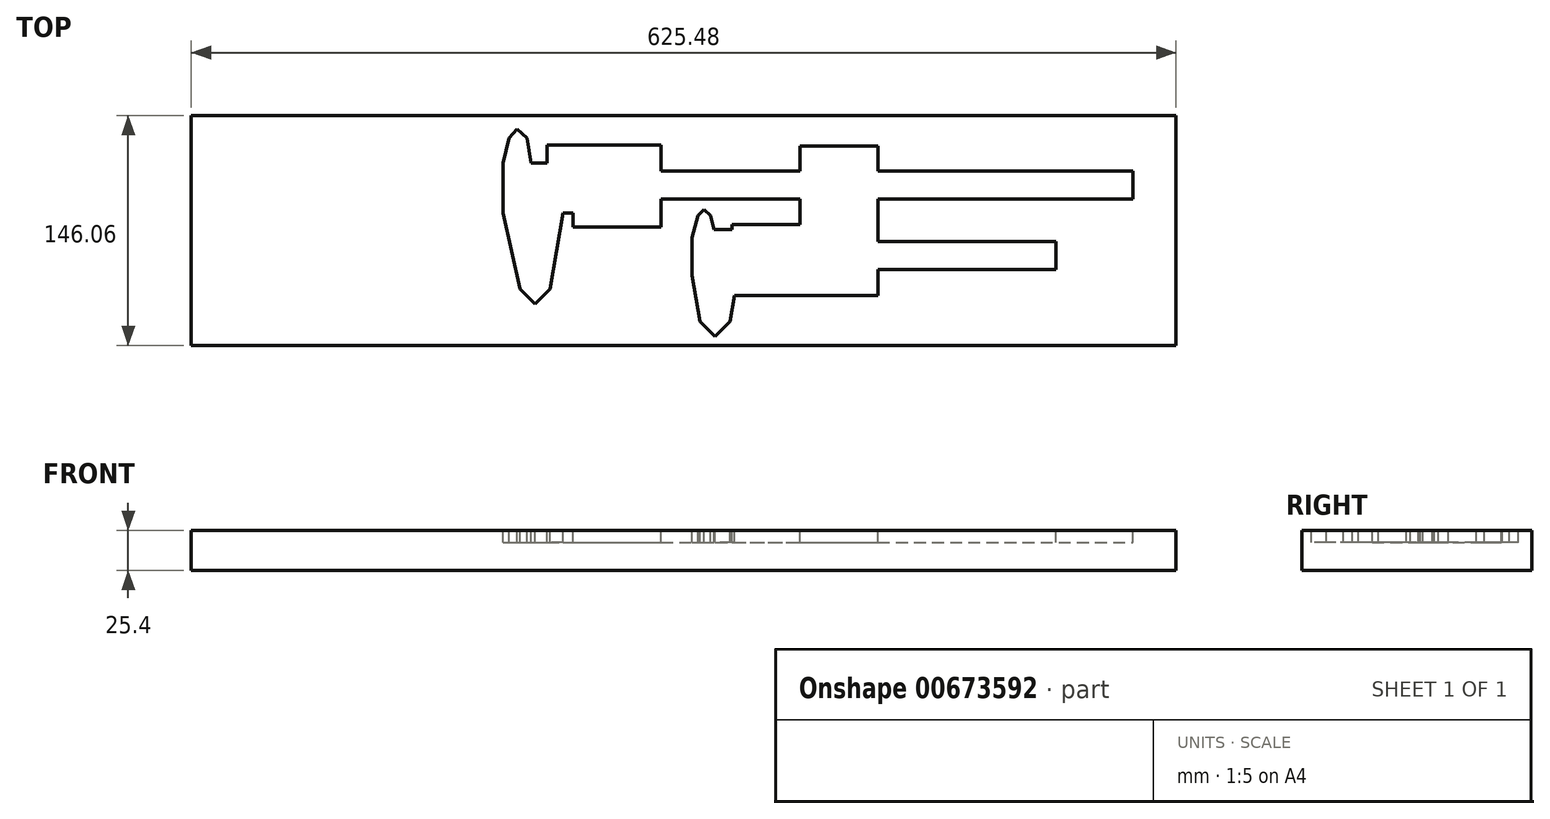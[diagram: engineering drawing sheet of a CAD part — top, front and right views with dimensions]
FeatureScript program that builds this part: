
annotation { "Feature Type Name" : "Feature", "Feature Type Description" : "" }
export const myFeature = defineFeature(function(context is Context, id is Id, definition is map)
    precondition{}
    {
        {
            var Q0;
            Q0=qCreatedBy(makeId("Top.planeOp"),FACE);
            var sketch = newSketch(context, id + "F0", { "sketchPlane" : qUnion([Q0])});
            skLineSegment(sketch, "E0.bottom", {"start": v(312.74, 73.03) * mm, "end": v(-312.74, 73.03) * mm});
            skLineSegment(sketch, "E0.top", {"start": v(312.74, -73.02) * mm, "end": v(-312.74, -73.02) * mm});
            skLineSegment(sketch, "E0.left", {"start": v(312.74, 73.03) * mm, "end": v(312.74, -73.02) * mm});
            skLineSegment(sketch, "E0.right", {"start": v(-312.74, 73.03) * mm, "end": v(-312.74, -73.02) * mm});
            skPoint(sketch, "E0.middle", {"position": v(0, 0) * mm});
            skSolve(sketch);
        }
        {
            var Q0;
            Q0=qCreatedBy(makeId("Top.planeOp"),FACE);
            var sketch = newSketch(context, id + "F1", { "sketchPlane" : qUnion([Q0])});
            skLineSegment(sketch, "E1", {"start": v(10.22, -57.71) * mm, "end": v(29.27, -57.71) * mm, "construction": true});
            skLineSegment(sketch, "E2", {"start": v(10.22, -57.71) * mm, "end": v(19.75, -67.24) * mm});
            skPoint(sketch, "E2.endSnap0", {"position": v(19.75, -57.71) * mm});
            skLineSegment(sketch, "E3", {"start": v(19.75, -67.24) * mm, "end": v(29.27, -57.71) * mm});
            skPoint(sketch, "E4", {"position": v(34.35, -28.5) * mm});
            skPoint(sketch, "E5", {"position": v(5.14, -28.5) * mm});
            skLineSegment(sketch, "E6", {"start": v(5.14, -28.5) * mm, "end": v(10.22, -57.71) * mm});
            skLineSegment(sketch, "E7", {"start": v(34.35, -28.5) * mm, "end": v(29.27, -57.71) * mm});
            skLineSegment(sketch, "E8", {"start": v(5.14, -28.5) * mm, "end": v(5.14, -4.37) * mm});
            skLineSegment(sketch, "E9", {"start": v(5.14, -4.37) * mm, "end": v(9.22, 9.6) * mm});
            skLineSegment(sketch, "E10", {"start": v(9.22, 9.6) * mm, "end": v(12.76, 13.4) * mm});
            skLineSegment(sketch, "E11", {"start": v(12.76, 13.4) * mm, "end": v(16.84, 9.6) * mm});
            skLineSegment(sketch, "E12", {"start": v(16.84, 9.6) * mm, "end": v(20.38, -4.37) * mm});
            skPoint(sketch, "E13", {"position": v(12.76, -4.37) * mm});
            skLineSegment(sketch, "E14", {"start": v(30.54, 3.75) * mm, "end": v(123.25, 3.75) * mm});
            skLineSegment(sketch, "E15", {"start": v(32.14, -41.2) * mm, "end": v(123.25, -41.2) * mm});
            skLineSegment(sketch, "E16.bottom", {"start": v(123.25, -6.91) * mm, "end": v(236.28, -6.91) * mm});
            skLineSegment(sketch, "E16.top", {"start": v(123.25, -24.7) * mm, "end": v(236.28, -24.7) * mm});
            skLineSegment(sketch, "E16.right", {"start": v(236.28, -6.91) * mm, "end": v(236.28, -24.7) * mm});
            skPoint(sketch, "E17", {"position": v(30.54, -4.37) * mm});
            skLineSegment(sketch, "E18", {"start": v(20.38, -4.37) * mm, "end": v(30.54, -4.37) * mm});
            skLineSegment(sketch, "E19", {"start": v(30.54, -4.37) * mm, "end": v(30.54, 3.75) * mm});
            skLineSegment(sketch, "E20", {"start": v(123.25, 3.75) * mm, "end": v(123.25, -6.91) * mm});
            skLineSegment(sketch, "E21", {"start": v(123.25, -24.7) * mm, "end": v(123.25, -41.2) * mm});
            skPoint(sketch, "E22", {"position": v(19.75, -28.5) * mm});
            skLineSegment(sketch, "E23", {"start": v(30.54, 0.7) * mm, "end": v(19.1, 0.7) * mm});
            skPoint(sketch, "E24", {"position": v(19.1, 0.7) * mm});
            skPoint(sketch, "E25", {"position": v(32.14, -41.2) * mm});
            skPoint(sketch, "E26", {"position": v(30.54, 0.7) * mm});
            skSolve(sketch);
        }
        {
            var Q0;
            Q0=qCreatedBy(makeId("Top.planeOp"),FACE);
            var sketch = newSketch(context, id + "F2", { "sketchPlane" : qUnion([Q0])});
            skLineSegment(sketch, "E27", {"start": v(-104.01, -37.14) * mm, "end": v(-84.96, -37.14) * mm, "construction": true});
            skLineSegment(sketch, "E28", {"start": v(-104.01, -37.14) * mm, "end": v(-94.49, -46.67) * mm});
            skPoint(sketch, "E28.endSnap0", {"position": v(-94.49, -37.14) * mm});
            skLineSegment(sketch, "E29", {"start": v(-94.49, -46.67) * mm, "end": v(-84.96, -37.14) * mm});
            skPoint(sketch, "E30", {"position": v(-76.54, 11.12) * mm});
            skPoint(sketch, "E31", {"position": v(-114.64, 11.12) * mm});
            skLineSegment(sketch, "E32", {"start": v(-114.64, 11.12) * mm, "end": v(-104.01, -37.14) * mm});
            skLineSegment(sketch, "E33", {"start": v(-76.54, 11.12) * mm, "end": v(-84.96, -37.14) * mm});
            skLineSegment(sketch, "E34", {"start": v(-114.64, 11.12) * mm, "end": v(-114.64, 42.87) * mm});
            skLineSegment(sketch, "E35", {"start": v(-114.64, 42.87) * mm, "end": v(-111.06, 58.76) * mm});
            skLineSegment(sketch, "E36", {"start": v(-111.06, 58.76) * mm, "end": v(-105.75, 64.46) * mm});
            skLineSegment(sketch, "E37", {"start": v(-105.75, 64.46) * mm, "end": v(-99.63, 58.76) * mm});
            skLineSegment(sketch, "E38", {"start": v(-99.63, 58.76) * mm, "end": v(-96.86, 42.87) * mm});
            skPoint(sketch, "E39", {"position": v(-105.75, 42.87) * mm});
            skLineSegment(sketch, "E40", {"start": v(-86.7, 54.3) * mm, "end": v(-14.31, 54.3) * mm});
            skLineSegment(sketch, "E41", {"start": v(-70.2, 2.23) * mm, "end": v(-14.31, 2.23) * mm});
            skLineSegment(sketch, "E42.bottom", {"start": v(-14.31, 37.79) * mm, "end": v(285.4, 37.79) * mm});
            skLineSegment(sketch, "E42.top", {"start": v(-14.31, 20) * mm, "end": v(285.4, 20) * mm});
            skLineSegment(sketch, "E42.right", {"start": v(285.4, 37.79) * mm, "end": v(285.4, 20) * mm});
            skPoint(sketch, "E43", {"position": v(-86.7, 42.87) * mm});
            skLineSegment(sketch, "E44", {"start": v(-96.86, 42.87) * mm, "end": v(-86.7, 42.87) * mm});
            skLineSegment(sketch, "E45", {"start": v(-86.7, 42.87) * mm, "end": v(-86.7, 54.3) * mm});
            skLineSegment(sketch, "E46", {"start": v(-14.31, 54.3) * mm, "end": v(-14.31, 37.79) * mm});
            skLineSegment(sketch, "E47", {"start": v(-14.31, 20) * mm, "end": v(-14.31, 2.23) * mm});
            skLineSegment(sketch, "E48.bottom", {"start": v(-76.54, 11.12) * mm, "end": v(-70.2, 11.12) * mm});
            skLineSegment(sketch, "E48.right", {"start": v(-70.2, 11.12) * mm, "end": v(-70.2, 2.23) * mm});
            skLineSegment(sketch, "E49.bottom", {"start": v(73.72, 3.75) * mm, "end": v(123.25, 3.75) * mm});
            skLineSegment(sketch, "E49.top", {"start": v(73.72, 53.66) * mm, "end": v(123.25, 53.66) * mm});
            skLineSegment(sketch, "E49.left", {"start": v(73.72, 3.75) * mm, "end": v(73.72, 53.66) * mm});
            skLineSegment(sketch, "E49.right", {"start": v(123.25, 3.75) * mm, "end": v(123.25, 53.66) * mm});
            skPoint(sketch, "E49.middle", {"position": v(98.49, 28.7) * mm});
            skSolve(sketch);
        }
        {
            var Q0;
            Q0=makeQuery(id+"F0.imprint","IMPRINT",FACE,{"disambiguationData":[TD([[makeQuery(id+"F0.imprint","IMPRINT",EDGE,{"derivedFrom":sQuery(id+"F0.wireOp",EDGE,"E0.bottom")}),1.0]])]});
            extrude(context, id + "F3", {"entities" : qUnion([Q0]), "depth" : -25.4 * mm, "offsetDistance" : 25.4 * mm});
        }
        {
            var Q0;
            Q0 = qSketchRegion(id + "F1", true);
            extrude(context, id + "F4", {"entities" : qUnion([Q0]), "operationType" : NewBodyOperationType.REMOVE, "depth" : -7.62 * mm, "offsetDistance" : 25.4 * mm});
        }
        {
            var Q0;
            Q0 = qSketchRegion(id + "F2", true);
            extrude(context, id + "F5", {"entities" : qUnion([Q0]), "operationType" : NewBodyOperationType.REMOVE, "oppositeDirection" : true, "depth" : 7.62 * mm, "offsetDistance" : 25.4 * mm});
        }
    });
